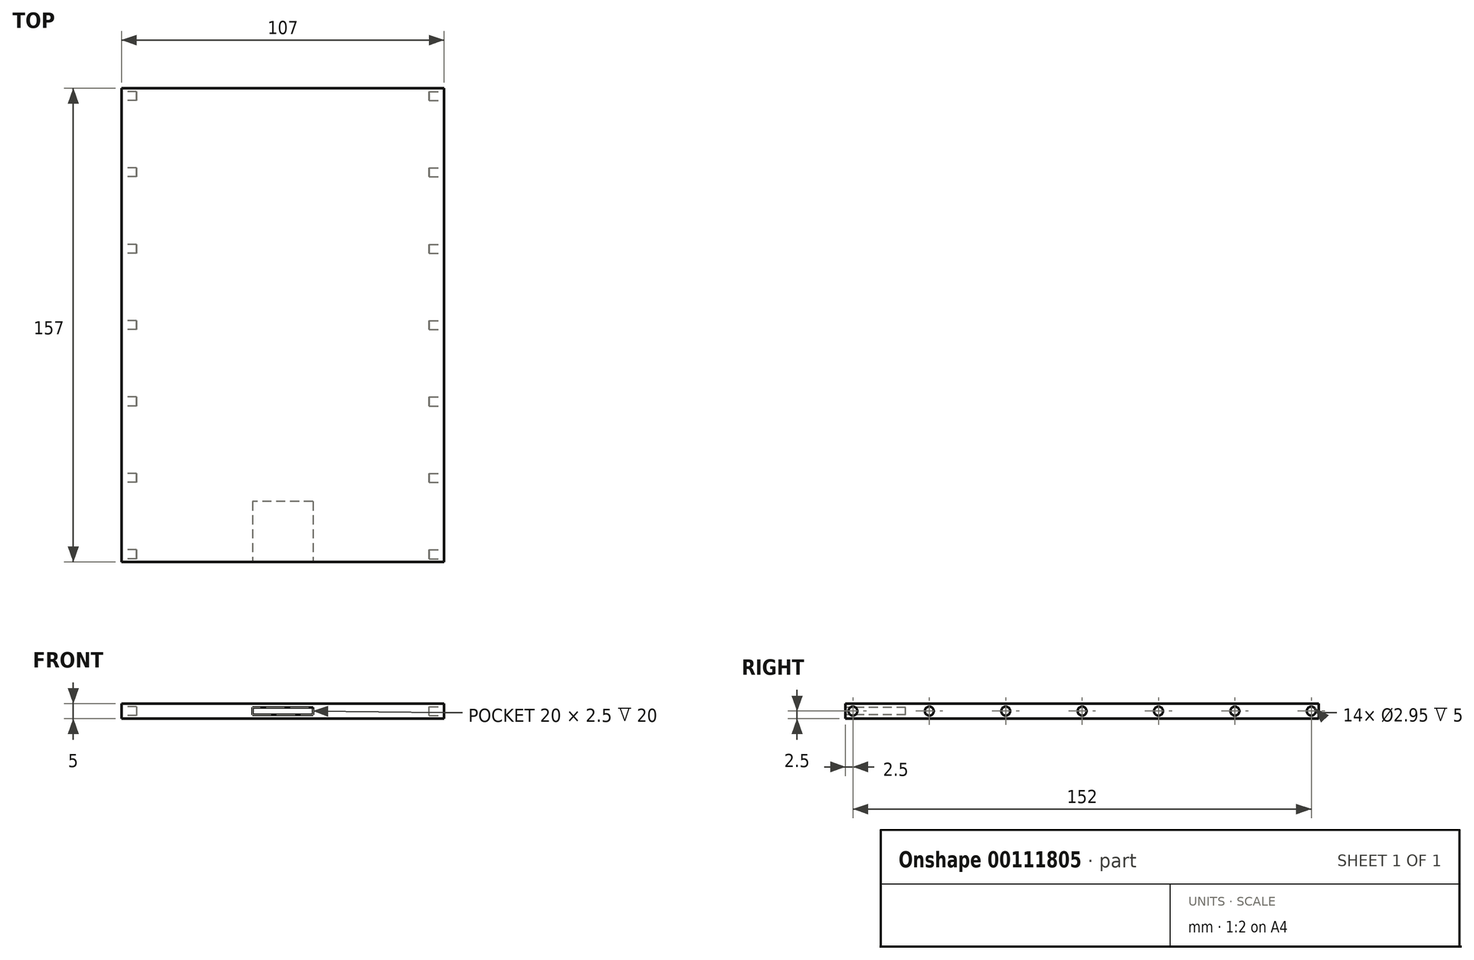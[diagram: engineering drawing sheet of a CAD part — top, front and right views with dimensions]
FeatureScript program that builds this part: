
annotation { "Feature Type Name" : "Feature", "Feature Type Description" : "" }
export const myFeature = defineFeature(function(context is Context, id is Id, definition is map)
    precondition{}
    {
        {
            var Q0;
            Q0=qCreatedBy(makeId("Top.planeOp"),FACE);
            var sketch = newSketch(context, id + "F0", { "sketchPlane" : qUnion([Q0])});
            skLineSegment(sketch, "E0.bottom", {"start": v(53.5, -78.5) * mm, "end": v(-53.5, -78.5) * mm});
            skLineSegment(sketch, "E0.top", {"start": v(53.5, 78.5) * mm, "end": v(-53.5, 78.5) * mm});
            skLineSegment(sketch, "E0.left", {"start": v(53.5, -78.5) * mm, "end": v(53.5, 78.5) * mm});
            skLineSegment(sketch, "E0.right", {"start": v(-53.5, -78.5) * mm, "end": v(-53.5, 78.5) * mm});
            skPoint(sketch, "E0.middle", {"position": v(0, 0) * mm});
            skSolve(sketch);
        }
        {
            var Q0;
            Q0 = qSketchRegion(id + "F0", true);
            extrude(context, id + "F1", {"entities" : qUnion([Q0]), "depth" : 5 * mm});
        }
        {
            var Q0;
            Q0=makeQuery(id+"F1.opExtrude","SWEPT_FACE",FACE,{"disambiguationData":[OSD([sQuery(id+"F0.wireOp",EDGE,"E0.left")])]});
            var sketch = newSketch(context, id + "F2", { "sketchPlane" : qUnion([Q0])});
            skCircle(sketch, "E1", {"center": v(-76, 2.5) * mm, "radius": 1.47 * mm});
            skCircle(sketch, "E2.1.0.0", {"center": v(-50.67, 2.5) * mm, "radius": 1.47 * mm});
            skCircle(sketch, "E2.2.0.0", {"center": v(-25.33, 2.5) * mm, "radius": 1.47 * mm});
            skCircle(sketch, "E2.3.0.0", {"center": v(0, 2.5) * mm, "radius": 1.47 * mm});
            skCircle(sketch, "E2.4.0.0", {"center": v(25.33, 2.5) * mm, "radius": 1.47 * mm});
            skCircle(sketch, "E2.5.0.0", {"center": v(50.67, 2.5) * mm, "radius": 1.47 * mm});
            skCircle(sketch, "E2.6.0.0", {"center": v(76, 2.5) * mm, "radius": 1.47 * mm});
            skLineSegment(sketch, "E2.direction1", {"start": v(-76, 2.5) * mm, "end": v(-50.67, 2.5) * mm, "construction": true});
            skSolve(sketch);
        }
        {
            var Q0;
            Q0 = qSketchRegion(id + "F2", true);
            extrude(context, id + "F3", {"entities" : qUnion([Q0]), "operationType" : NewBodyOperationType.REMOVE, "oppositeDirection" : true, "depth" : 5 * mm});
        }
        {
            var Q0;
            Q0=makeQuery(id+"F1.opExtrude","SWEPT_FACE",FACE,{"disambiguationData":[OSD([sQuery(id+"F0.wireOp",EDGE,"E0.right")])]});
            var sketch = newSketch(context, id + "F4", { "sketchPlane" : qUnion([Q0])});
            skCircle(sketch, "E3", {"center": v(-76, 2.5) * mm, "radius": 1.47 * mm});
            skCircle(sketch, "E4.1.0.0", {"center": v(-50.67, 2.5) * mm, "radius": 1.47 * mm});
            skCircle(sketch, "E4.2.0.0", {"center": v(-25.33, 2.5) * mm, "radius": 1.47 * mm});
            skCircle(sketch, "E4.3.0.0", {"center": v(0, 2.5) * mm, "radius": 1.47 * mm});
            skCircle(sketch, "E4.4.0.0", {"center": v(25.33, 2.5) * mm, "radius": 1.47 * mm});
            skCircle(sketch, "E4.5.0.0", {"center": v(50.67, 2.5) * mm, "radius": 1.47 * mm});
            skCircle(sketch, "E4.6.0.0", {"center": v(76, 2.5) * mm, "radius": 1.47 * mm});
            skLineSegment(sketch, "E4.direction1", {"start": v(-76, 2.5) * mm, "end": v(-50.67, 2.5) * mm, "construction": true});
            skSolve(sketch);
        }
        {
            var Q0;
            Q0 = qSketchRegion(id + "F4", true);
            extrude(context, id + "F5", {"entities" : qUnion([Q0]), "operationType" : NewBodyOperationType.REMOVE, "oppositeDirection" : true, "depth" : 5 * mm});
        }
        {
            var Q0;
            Q0=makeQuery(id+"F1.opExtrude","SWEPT_FACE",FACE,{"disambiguationData":[OSD([sQuery(id+"F0.wireOp",EDGE,"E0.bottom")])]});
            var sketch = newSketch(context, id + "F6", { "sketchPlane" : qUnion([Q0])});
            skLineSegment(sketch, "E5.bottom", {"start": v(10, 1.25) * mm, "end": v(-10, 1.25) * mm});
            skLineSegment(sketch, "E5.top", {"start": v(10, 3.75) * mm, "end": v(-10, 3.75) * mm});
            skLineSegment(sketch, "E5.left", {"start": v(10, 1.25) * mm, "end": v(10, 3.75) * mm});
            skLineSegment(sketch, "E5.right", {"start": v(-10, 1.25) * mm, "end": v(-10, 3.75) * mm});
            skPoint(sketch, "E5.middle", {"position": v(0, 2.5) * mm});
            skSolve(sketch);
        }
        {
            var Q0;
            Q0=makeQuery(id+"F6.imprint","IMPRINT",FACE,{"disambiguationData":[TD([[makeQuery(id+"F6.imprint","IMPRINT",EDGE,{"derivedFrom":sQuery(id+"F6.wireOp",EDGE,"E5.bottom")}),-1.0]])]});
            extrude(context, id + "F7", {"entities" : qUnion([Q0]), "operationType" : NewBodyOperationType.REMOVE, "oppositeDirection" : true, "depth" : 20 * mm});
        }
    });
